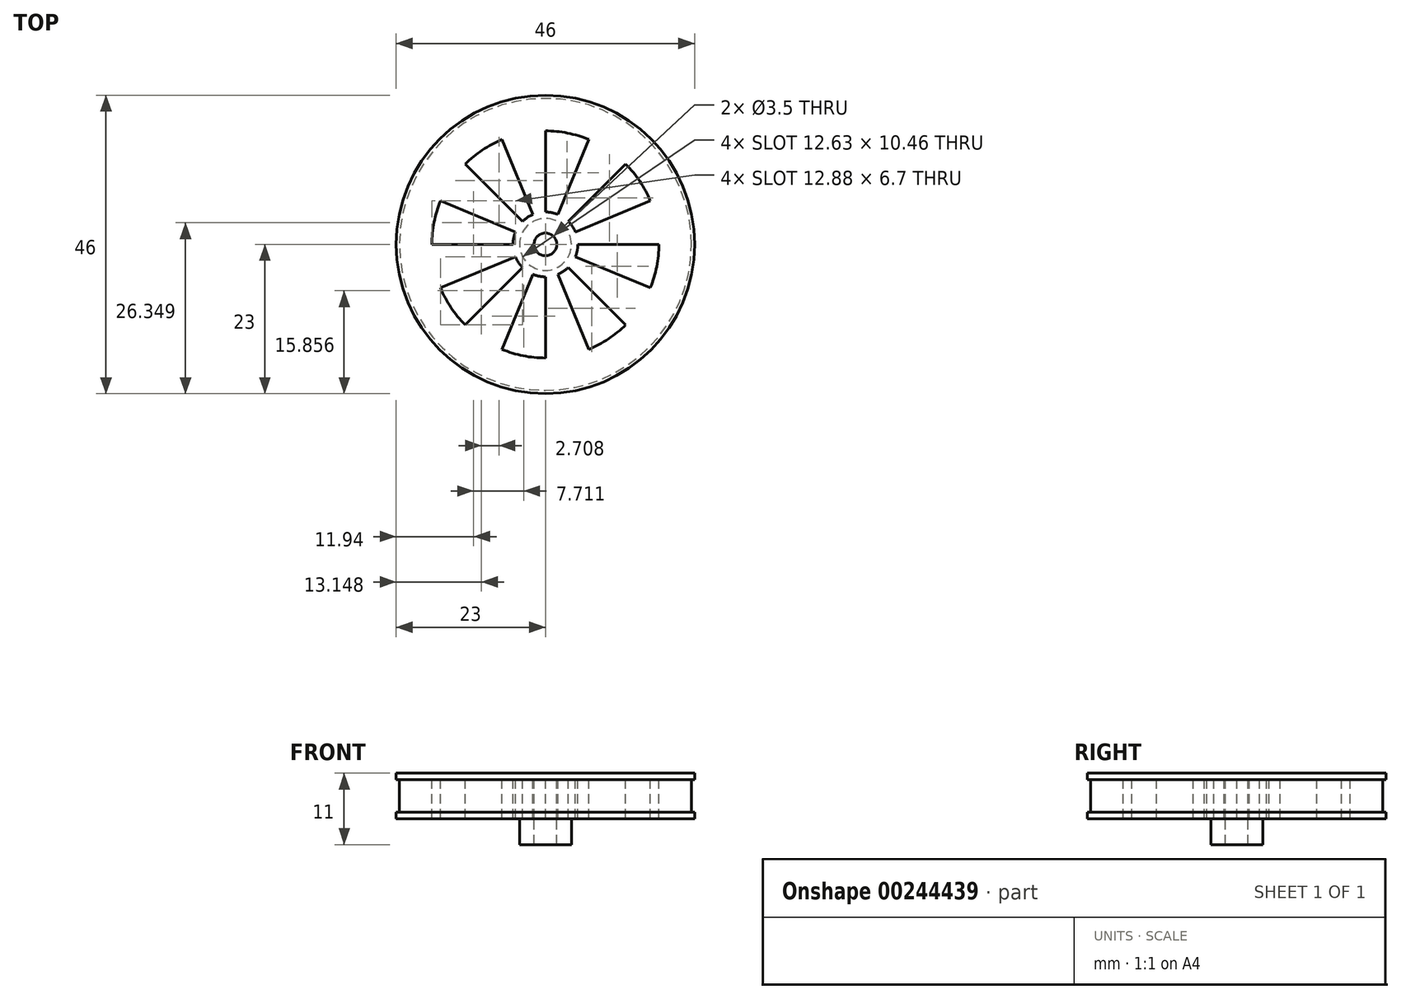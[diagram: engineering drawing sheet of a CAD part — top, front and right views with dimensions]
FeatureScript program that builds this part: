
annotation { "Feature Type Name" : "Feature", "Feature Type Description" : "" }
export const myFeature = defineFeature(function(context is Context, id is Id, definition is map)
    precondition{}
    {
        {
            var Q0;
            Q0=qCreatedBy(makeId("Top.planeOp"),FACE);
            var sketch = newSketch(context, id + "F0", { "sketchPlane" : qUnion([Q0])});
            skCircle(sketch, "E0", {"center": v(0, 0) * mm, "radius": 23 * mm});
            skSolve(sketch);
        }
        {
            var Q0;
            Q0=makeQuery(id+"F0.imprint","IMPRINT",FACE,{"disambiguationData":[TD([[makeQuery(id+"F0.imprint","IMPRINT",EDGE,{"derivedFrom":sQuery(id+"F0.wireOp",EDGE,"E0")}),1.0]])]});
            extrude(context, id + "F1", {"entities" : qUnion([Q0]), "depth" : 1 * mm});
        }
        {
            var Q0;
            Q0=makeQuery(id+"F1.opExtrude","CAP_FACE",FACE,{"disambiguationData":[OSD([sQuery(id+"F0.wireOp",EDGE,"E0")])],"isStart":false});
            var sketch = newSketch(context, id + "F2", { "sketchPlane" : qUnion([Q0])});
            skCircle(sketch, "E1", {"center": v(0, 0) * mm, "radius": 23 * mm});
            skCircle(sketch, "E2", {"center": v(0, 0) * mm, "radius": 22.5 * mm});
            skSolve(sketch);
        }
        {
            var Q0;
            Q0=makeQuery(id+"F2.imprint","IMPRINT",FACE,{"disambiguationData":[TD([[makeQuery(id+"F2.imprint","IMPRINT",EDGE,{"derivedFrom":sQuery(id+"F2.wireOp",EDGE,"E2")}),1.0]])]});
            extrude(context, id + "F3", {"entities" : qUnion([Q0]), "operationType" : NewBodyOperationType.ADD, "depth" : 5 * mm});
        }
        {
            var Q0;
            Q0=makeQuery(id+"F3.opExtrude","CAP_FACE",FACE,{"disambiguationData":[OSD([sQuery(id+"F2.wireOp",EDGE,"E2")])],"isStart":false});
            var sketch = newSketch(context, id + "F4", { "sketchPlane" : qUnion([Q0])});
            skCircle(sketch, "E3.0.0", {"center": v(0, 0) * mm, "radius": 22.5 * mm});
            skCircle(sketch, "E4", {"center": v(0, 0) * mm, "radius": 23 * mm});
            skSolve(sketch);
        }
        {
            var Q0;
            Q0=makeQuery(id+"F4.imprint","IMPRINT",FACE,{"disambiguationData":[TD([[makeQuery(id+"F4.imprint","IMPRINT",EDGE,{"derivedFrom":sQuery(id+"F4.wireOp",EDGE,"E3.0.0")}),-1.0]])]});
            var Q1;
            Q1=makeQuery(id+"F4.imprint","IMPRINT",FACE,{"disambiguationData":[TD([[makeQuery(id+"F4.imprint","IMPRINT",EDGE,{"derivedFrom":sQuery(id+"F4.wireOp",EDGE,"E3.0.0")}),1.0]])]});
            extrude(context, id + "F5", {"entities" : qUnion([Q0, Q1]), "operationType" : NewBodyOperationType.ADD, "depth" : 1 * mm});
        }
        {
            var Q0;
            Q0=makeQuery(id+"F5.opExtrude","CAP_FACE",FACE,{"disambiguationData":[OSD([sQuery(id+"F4.wireOp",EDGE,"E4")])],"isStart":false});
            var sketch = newSketch(context, id + "F6", { "sketchPlane" : qUnion([Q0])});
            skCircle(sketch, "E5.0.0", {"center": v(0, 0) * mm, "radius": 23 * mm});
            skCircle(sketch, "E6", {"center": v(0, 0) * mm, "radius": 1.75 * mm});
            skSolve(sketch);
        }
        {
            var Q0;
            Q0=makeQuery(id+"F6.imprint","IMPRINT",FACE,{"disambiguationData":[TD([[makeQuery(id+"F6.imprint","IMPRINT",EDGE,{"derivedFrom":sQuery(id+"F6.wireOp",EDGE,"E6")}),1.0]])]});
            extrude(context, id + "F7", {"entities" : qUnion([Q0]), "operationType" : NewBodyOperationType.REMOVE, "oppositeDirection" : true, "depth" : 25 * mm});
        }
        {
            var Q0;
            Q0=makeQuery(id+"F5.opExtrude","CAP_FACE",FACE,{"disambiguationData":[OSD([sQuery(id+"F4.wireOp",EDGE,"E4")])],"isStart":false});
            var sketch = newSketch(context, id + "F8", { "sketchPlane" : qUnion([Q0])});
            skCircle(sketch, "E7.0.0", {"center": v(0, 0) * mm, "radius": 23 * mm});
            skCircle(sketch, "E8", {"center": v(0, 0) * mm, "radius": 5 * mm});
            skCircle(sketch, "E9", {"center": v(0, 0) * mm, "radius": 17.5 * mm});
            skLineSegment(sketch, "E10", {"start": v(0, 0) * mm, "end": v(0, 17.5) * mm});
            skLineSegment(sketch, "E11", {"start": v(0, 0) * mm, "end": v(6.7, 16.17) * mm});
            skLineSegment(sketch, "E12", {"start": v(0, 0) * mm, "end": v(-6.7, 16.17) * mm});
            skLineSegment(sketch, "E13", {"start": v(0, 0) * mm, "end": v(-12.37, 12.37) * mm});
            skLineSegment(sketch, "E14", {"start": v(0, 0) * mm, "end": v(-16.17, 6.7) * mm});
            skLineSegment(sketch, "E15", {"start": v(0, 0) * mm, "end": v(-17.5, 0) * mm});
            skLineSegment(sketch, "E16", {"start": v(0, 0) * mm, "end": v(-16.17, -6.7) * mm});
            skLineSegment(sketch, "E17", {"start": v(0, 0) * mm, "end": v(-12.37, -12.37) * mm});
            skLineSegment(sketch, "E18", {"start": v(0, 0) * mm, "end": v(-6.7, -16.17) * mm});
            skLineSegment(sketch, "E19", {"start": v(0, 0) * mm, "end": v(0, -17.5) * mm});
            skLineSegment(sketch, "E20", {"start": v(0, 0) * mm, "end": v(6.7, -16.17) * mm});
            skLineSegment(sketch, "E21", {"start": v(0, 0) * mm, "end": v(12.37, -12.37) * mm});
            skLineSegment(sketch, "E22", {"start": v(0, 0) * mm, "end": v(16.17, -6.7) * mm});
            skLineSegment(sketch, "E23", {"start": v(0, 0) * mm, "end": v(17.5, 0) * mm});
            skLineSegment(sketch, "E24", {"start": v(0, 0) * mm, "end": v(16.17, 6.7) * mm});
            skLineSegment(sketch, "E25", {"start": v(0, 0) * mm, "end": v(12.37, 12.37) * mm});
            skSolve(sketch);
        }
        {
            var Q0;
            {var subQ0=sQuery(id+"F8.wireOp",EDGE,"E10");var subQ1=sQuery(id+"F8.wireOp",EDGE,"E8");var subQ2=makeQuery(id+"F8.imprint","INTERSECT",VERTEX,{"derivedFrom":[subQ1,subQ0]});Q0=makeQuery(id+"F8.imprint","IMPRINT",FACE,{"disambiguationData":[TD([[makeQuery(id+"F8.imprint","IMPRINT",EDGE,{"disambiguationData":[TD([[subQ2,1.0]])],"derivedFrom":subQ1}),-1.0]])]});}
            var Q1;
            {var subQ0=sQuery(id+"F8.wireOp",EDGE,"E24");var subQ1=sQuery(id+"F8.wireOp",EDGE,"E8");var subQ2=makeQuery(id+"F8.imprint","INTERSECT",VERTEX,{"derivedFrom":[subQ1,subQ0]});Q1=makeQuery(id+"F8.imprint","IMPRINT",FACE,{"disambiguationData":[TD([[makeQuery(id+"F8.imprint","IMPRINT",EDGE,{"disambiguationData":[TD([[subQ2,-1.0]])],"derivedFrom":subQ1}),-1.0]])]});}
            var Q2;
            {var subQ0=sQuery(id+"F8.wireOp",EDGE,"E23");var subQ1=sQuery(id+"F8.wireOp",EDGE,"E8");var subQ2=makeQuery(id+"F8.imprint","INTERSECT",VERTEX,{"derivedFrom":[subQ1,subQ0]});Q2=makeQuery(id+"F8.imprint","IMPRINT",FACE,{"disambiguationData":[TD([[makeQuery(id+"F8.imprint","IMPRINT",EDGE,{"disambiguationData":[TD([[subQ2,1.0]])],"derivedFrom":subQ1}),-1.0]])]});}
            var Q3;
            {var subQ0=sQuery(id+"F8.wireOp",EDGE,"E20");var subQ1=sQuery(id+"F8.wireOp",EDGE,"E8");var subQ2=makeQuery(id+"F8.imprint","INTERSECT",VERTEX,{"derivedFrom":[subQ1,subQ0]});Q3=makeQuery(id+"F8.imprint","IMPRINT",FACE,{"disambiguationData":[TD([[makeQuery(id+"F8.imprint","IMPRINT",EDGE,{"disambiguationData":[TD([[subQ2,-1.0]])],"derivedFrom":subQ1}),-1.0]])]});}
            var Q4;
            {var subQ0=sQuery(id+"F8.wireOp",EDGE,"E18");var subQ1=sQuery(id+"F8.wireOp",EDGE,"E8");var subQ2=makeQuery(id+"F8.imprint","INTERSECT",VERTEX,{"derivedFrom":[subQ1,subQ0]});Q4=makeQuery(id+"F8.imprint","IMPRINT",FACE,{"disambiguationData":[TD([[makeQuery(id+"F8.imprint","IMPRINT",EDGE,{"disambiguationData":[TD([[subQ2,-1.0]])],"derivedFrom":subQ1}),-1.0]])]});}
            var Q5;
            {var subQ0=sQuery(id+"F8.wireOp",EDGE,"E16");var subQ1=sQuery(id+"F8.wireOp",EDGE,"E8");var subQ2=makeQuery(id+"F8.imprint","INTERSECT",VERTEX,{"derivedFrom":[subQ1,subQ0]});Q5=makeQuery(id+"F8.imprint","IMPRINT",FACE,{"disambiguationData":[TD([[makeQuery(id+"F8.imprint","IMPRINT",EDGE,{"disambiguationData":[TD([[subQ2,-1.0]])],"derivedFrom":subQ1}),-1.0]])]});}
            var Q6;
            {var subQ0=sQuery(id+"F8.wireOp",EDGE,"E14");var subQ1=sQuery(id+"F8.wireOp",EDGE,"E8");var subQ2=makeQuery(id+"F8.imprint","INTERSECT",VERTEX,{"derivedFrom":[subQ1,subQ0]});Q6=makeQuery(id+"F8.imprint","IMPRINT",FACE,{"disambiguationData":[TD([[makeQuery(id+"F8.imprint","IMPRINT",EDGE,{"disambiguationData":[TD([[subQ2,-1.0]])],"derivedFrom":subQ1}),-1.0]])]});}
            var Q7;
            {var subQ0=sQuery(id+"F8.wireOp",EDGE,"E12");var subQ1=sQuery(id+"F8.wireOp",EDGE,"E8");var subQ2=makeQuery(id+"F8.imprint","INTERSECT",VERTEX,{"derivedFrom":[subQ1,subQ0]});Q7=makeQuery(id+"F8.imprint","IMPRINT",FACE,{"disambiguationData":[TD([[makeQuery(id+"F8.imprint","IMPRINT",EDGE,{"disambiguationData":[TD([[subQ2,-1.0]])],"derivedFrom":subQ1}),-1.0]])]});}
            extrude(context, id + "F9", {"entities" : qUnion([Q0, Q1, Q2, Q3, Q4, Q5, Q6, Q7]), "operationType" : NewBodyOperationType.REMOVE, "oppositeDirection" : true, "depth" : 10 * mm});
        }
        {
            var Q0;
            Q0=makeQuery(id+"F1.opExtrude","CAP_FACE",FACE,{"disambiguationData":[OSD([sQuery(id+"F0.wireOp",EDGE,"E0")])],"isStart":true});
            var sketch = newSketch(context, id + "F10", { "sketchPlane" : qUnion([Q0])});
            skCircle(sketch, "E26", {"center": v(0, 0) * mm, "radius": 4 * mm});
            skSolve(sketch);
        }
        {
            var Q0;
            Q0=makeQuery(id+"F10.imprint","IMPRINT",FACE,{"disambiguationData":[TD([[makeQuery(id+"F10.imprint","IMPRINT",EDGE,{"derivedFrom":sQuery(id+"F10.wireOp",EDGE,"E26")}),1.0]])]});
            extrude(context, id + "F11", {"entities" : qUnion([Q0]), "depth" : 4 * mm});
        }
    });
